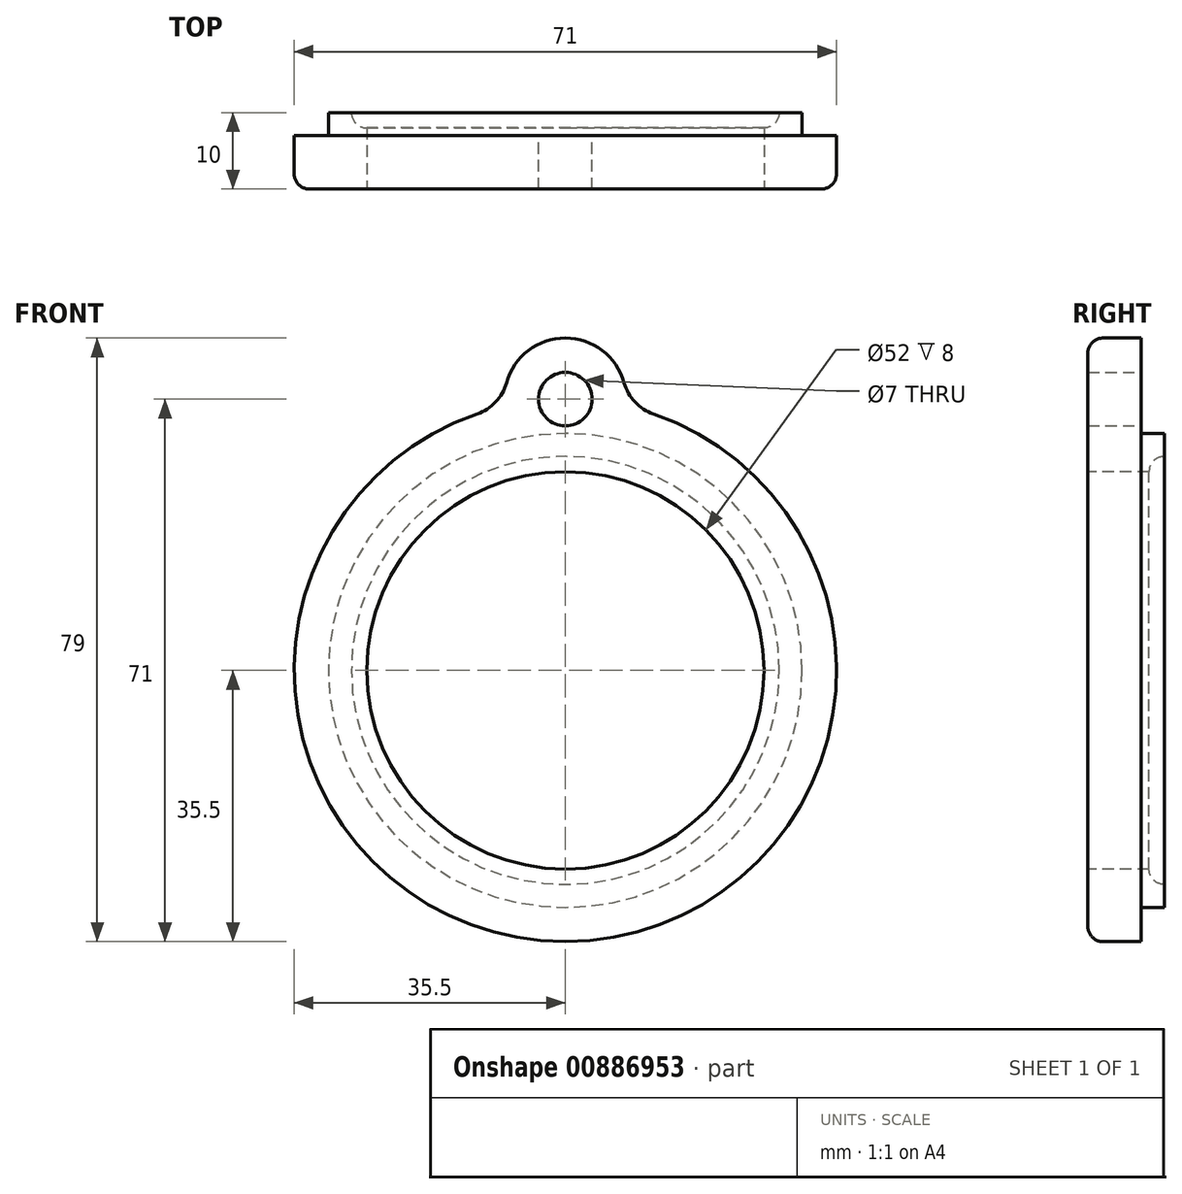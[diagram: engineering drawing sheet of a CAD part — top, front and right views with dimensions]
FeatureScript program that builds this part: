
annotation { "Feature Type Name" : "Feature", "Feature Type Description" : "" }
export const myFeature = defineFeature(function(context is Context, id is Id, definition is map)
    precondition{}
    {
        {
            var Q0;
            Q0=qCreatedBy(makeId("Right.planeOp"),FACE);
            var sketch = newSketch(context, id + "F0", { "sketchPlane" : qUnion([Q0])});
            skLineSegment(sketch, "E0", {"start": v(-8.7, 0) * mm, "end": v(23.28, 0) * mm, "construction": true});
            skLineSegment(sketch, "E1", {"start": v(0, 26) * mm, "end": v(0, 35.5) * mm});
            skLineSegment(sketch, "E2", {"start": v(0, 35.5) * mm, "end": v(7, 35.5) * mm});
            skLineSegment(sketch, "E3", {"start": v(7, 35.5) * mm, "end": v(7, 31) * mm});
            skLineSegment(sketch, "E4", {"start": v(7, 31) * mm, "end": v(10, 31) * mm});
            skLineSegment(sketch, "E5", {"start": v(10, 31) * mm, "end": v(10, 28) * mm});
            skLineSegment(sketch, "E6", {"start": v(8, 26) * mm, "end": v(0, 26) * mm});
            skArc(sketch, "E7", {"start": v(10, 28) * mm, "mid": v(8.59, 27.41) * mm, "end": v(8, 26) * mm});
            skSolve(sketch);
        }
        {
            var Q0;
            Q0 = qSketchRegion(id + "F0", true);
            var Q1;
            Q1=sQuery(id+"F0.wireOp",EDGE,"E0");
            revolve(context, id + "F1", {"surfaceOperationType" : NewSurfaceOperationType.NEW, "entities" : qUnion([Q0]), "axis" : qUnion([Q1]), "revolveType" : RevolveType.FULL});
        }
        {
            var Q0;
            Q0=makeQuery(id+"F1.opRevolve","SWEPT_FACE",FACE,{"disambiguationData":[OSD([sQuery(id+"F0.wireOp",EDGE,"E3")])]});
            var sketch = newSketch(context, id + "F2", { "sketchPlane" : qUnion([Q0])});
            skCircle(sketch, "E8", {"center": v(0, 35.5) * mm, "radius": 8 * mm});
            skSolve(sketch);
        }
        {
            var Q0;
            Q0 = qSketchRegion(id + "F2", true);
            var Q1;
            Q1=makeQuery(id+"F1.opRevolve","SWEPT_FACE",FACE,{"disambiguationData":[OSD([sQuery(id+"F0.wireOp",EDGE,"E1")])]});
            extrude(context, id + "F3", {"entities" : qUnion([Q0]), "operationType" : NewBodyOperationType.ADD, "endBound" : BoundingType.UP_TO_SURFACE, "oppositeDirection" : true, "depth" : 25 * mm, "endBoundEntityFace" : qUnion([Q1]), "offsetDistance" : 25 * mm});
        }
        {
            var Q0;
            Q0=makeQuery(id+"F3.boolean.opBoolean","INTERSECT",EDGE,{"disambiguationData":[OD(1.0)],"derivedFrom":[makeQuery(id+"F1.opRevolve","SWEPT_FACE",FACE,{"disambiguationData":[OSD([sQuery(id+"F0.wireOp",EDGE,"E2")])]}),makeQuery(id+"F3.opExtrude","SWEPT_FACE",FACE,{"disambiguationData":[OSD([sQuery(id+"F2.wireOp",EDGE,"E8")])]})]});
            var Q1;
            Q1=makeQuery(id+"F3.boolean.opBoolean","INTERSECT",EDGE,{"disambiguationData":[OD(0.0)],"derivedFrom":[makeQuery(id+"F1.opRevolve","SWEPT_FACE",FACE,{"disambiguationData":[OSD([sQuery(id+"F0.wireOp",EDGE,"E2")])]}),makeQuery(id+"F3.opExtrude","SWEPT_FACE",FACE,{"disambiguationData":[OSD([sQuery(id+"F2.wireOp",EDGE,"E8")])]})]});
            fillet(context, id + "F4", {"entities" : qUnion([Q0, Q1]), "radius" : 6 * mm, "tangentPropagation" : true, "allowEdgeOverflow" : false});
        }
        {
            var Q0;
            Q0=sQuery(id+"F2.wireOp",VERTEX,"E8.center");
            var Q1;
            Q1=makeQuery(id+"F1.opRevolve","SWEPT_BODY",BODY,{"disambiguationData":[OSD([sQuery(id+"F0.wireOp",EDGE,"E1"),sQuery(id+"F0.wireOp",EDGE,"E2"),sQuery(id+"F0.wireOp",EDGE,"E3"),sQuery(id+"F0.wireOp",EDGE,"E4"),sQuery(id+"F0.wireOp",EDGE,"E5"),sQuery(id+"F0.wireOp",EDGE,"E6"),sQuery(id+"F0.wireOp",EDGE,"E7")])]});
            hole(context, id + "F5", {"style" : HoleStyle.SIMPLE, "endStyle" : HoleEndStyle.THROUGH, "holeDiameter" : 7 * mm, "majorDiameter" : 5 * mm, "tappedDepth" : 12 * mm, "tapClearance" : 3, "startFromSketch" : true, "locations" : qUnion([Q0]), "scope" : qUnion([Q1])});
        }
        {
            var Q0;
            Q0=makeQuery(id+"F3.opExtrude","CAP_EDGE",EDGE,{"disambiguationData":[OSD([sQuery(id+"F2.wireOp",EDGE,"E8")])],"isStart":false});
            fillet(context, id + "F6", {"entities" : qUnion([Q0]), "radius" : 2 * mm, "tangentPropagation" : true, "allowEdgeOverflow" : false});
        }
    });
